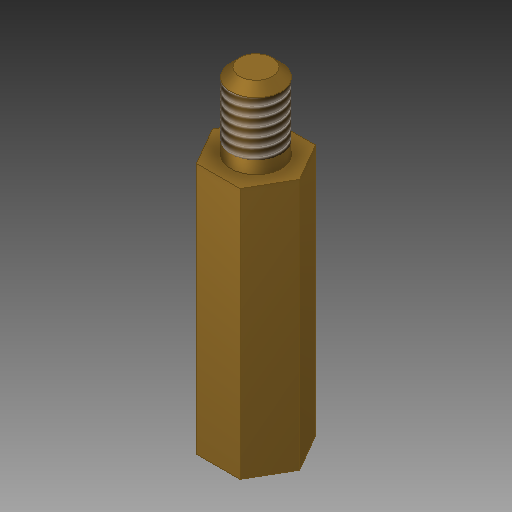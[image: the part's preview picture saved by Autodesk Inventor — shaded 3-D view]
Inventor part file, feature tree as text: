
AUTODESK INVENTOR PART (.ipt)
format: ipt  version: 2018 (Build 220112000, 112)  size: 130,560 bytes
history: native  units: mm
features: sketch x2, extrude x2, hole x1, thread x1, chamfer x1
ambient origin geometry x8: Origin, YZ Plane, XZ Plane, XY Plane, X Axis, Y Axis, Z Axis, Center Point
bodies: Solid1 (feature_tree)
feature tree (7):
  sketch  "Sketch1"  dims[d0=3.0mm d1=20.0mm d2=0.0mm]
  extrude  "Extrusion1"  Depth=20.0mm TaperAngle=0.0deg
  hole  "Hole2"  [1 undecoded]
  extrude  "Extrusion2"  Depth=6.0mm TaperAngle=0.0deg
  thread  "Thread1"  [1 undecoded]
  chamfer  "Chamfer1"  Distance=2.0mm Angle=45.0deg
  sketch  "Sketch3"  dims[d10=3.242mm d11=8.0mm d12=4.0mm d13=2.0mm d14=90.0deg d15=11.8mm d16=20.594885mm d17=4.0mm d18=6.0mm d19=0.0mm d20=5.0mm d21=0.0mm d22=0.7mm d23=2.0mm d24=45.0deg]
note: 2 required parameter values undecoded (feature->parameter linkage not recoverable at this tier; creation-order binding heuristic only, values carry confidence <= 0.55)
